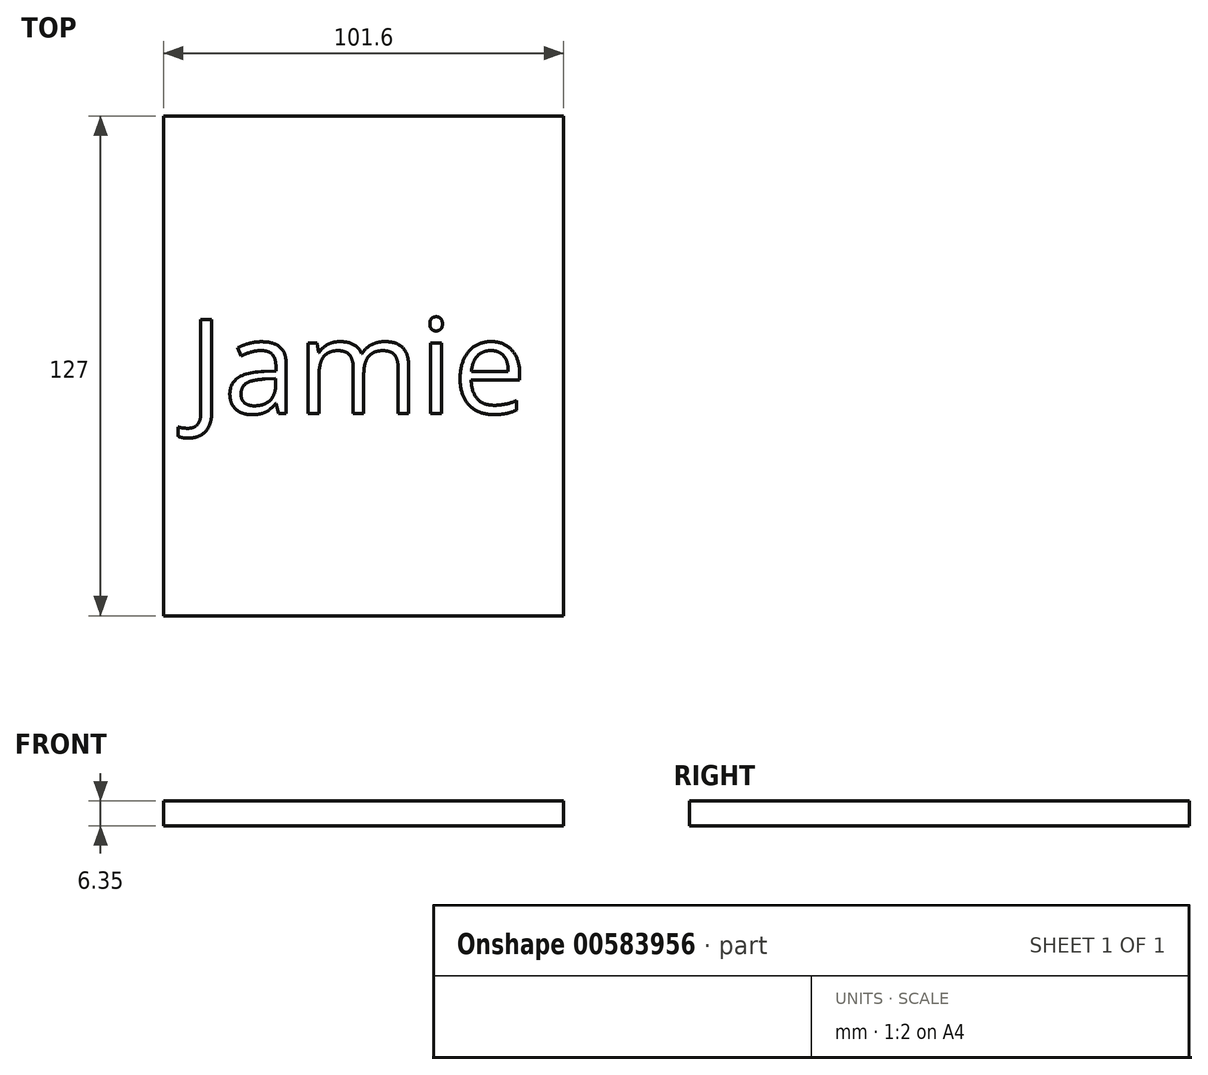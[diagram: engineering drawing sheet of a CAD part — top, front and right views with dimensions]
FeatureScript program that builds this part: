
annotation { "Feature Type Name" : "Feature", "Feature Type Description" : "" }
export const myFeature = defineFeature(function(context is Context, id is Id, definition is map)
    precondition{}
    {
        {
            var Q0;
            Q0=qCreatedBy(makeId("Top.planeOp"),FACE);
            var sketch = newSketch(context, id + "F0", { "sketchPlane" : qUnion([Q0])});
            skLineSegment(sketch, "E0.bottom", {"start": v(-50.8, 63.5) * mm, "end": v(50.8, 63.5) * mm});
            skLineSegment(sketch, "E0.top", {"start": v(-50.8, -63.5) * mm, "end": v(50.8, -63.5) * mm});
            skLineSegment(sketch, "E0.left", {"start": v(-50.8, 63.5) * mm, "end": v(-50.8, -63.5) * mm});
            skLineSegment(sketch, "E0.right", {"start": v(50.8, 63.5) * mm, "end": v(50.8, -63.5) * mm});
            skSolve(sketch);
        }
        {
            var Q0;
            Q0=makeQuery(id+"F0.imprint","IMPRINT",FACE,{"disambiguationData":[TD([[makeQuery(id+"F0.imprint","IMPRINT",EDGE,{"derivedFrom":sQuery(id+"F0.wireOp",EDGE,"E0.bottom")}),-1.0]])]});
            extrude(context, id + "F1", {"entities" : qUnion([Q0]), "depth" : 6.35 * mm, "offsetDistance" : 25.4 * mm});
        }
        {
            var Q0;
            Q0=makeQuery(id+"F1.opExtrude","CAP_FACE",FACE,{"disambiguationData":[OSD([sQuery(id+"F0.wireOp",EDGE,"E0.bottom"),sQuery(id+"F0.wireOp",EDGE,"E0.top"),sQuery(id+"F0.wireOp",EDGE,"E0.left"),sQuery(id+"F0.wireOp",EDGE,"E0.right")])],"isStart":false});
            var sketch = newSketch(context, id + "F2", { "sketchPlane" : qUnion([Q0])});
            skText(sketch, "E1", { "text": "Jamie", "fontName": "OpenSans-Regular.ttf"});
            const initialGuessF2  = {"E1": [-0.04445, -0.01204, 1, 0, 0.02408]};
            skSetInitialGuess(sketch, initialGuessF2);
            skSolve(sketch);
        }
        {
            var Q0;
            Q0 = qSketchRegion(id + "F2", true);
            extrude(context, id + "F3", {"entities" : qUnion([Q0]), "operationType" : NewBodyOperationType.ADD, "depth" : 1 / 203.2 * mm, "offsetDistance" : 25.4 * mm});
        }
    });
